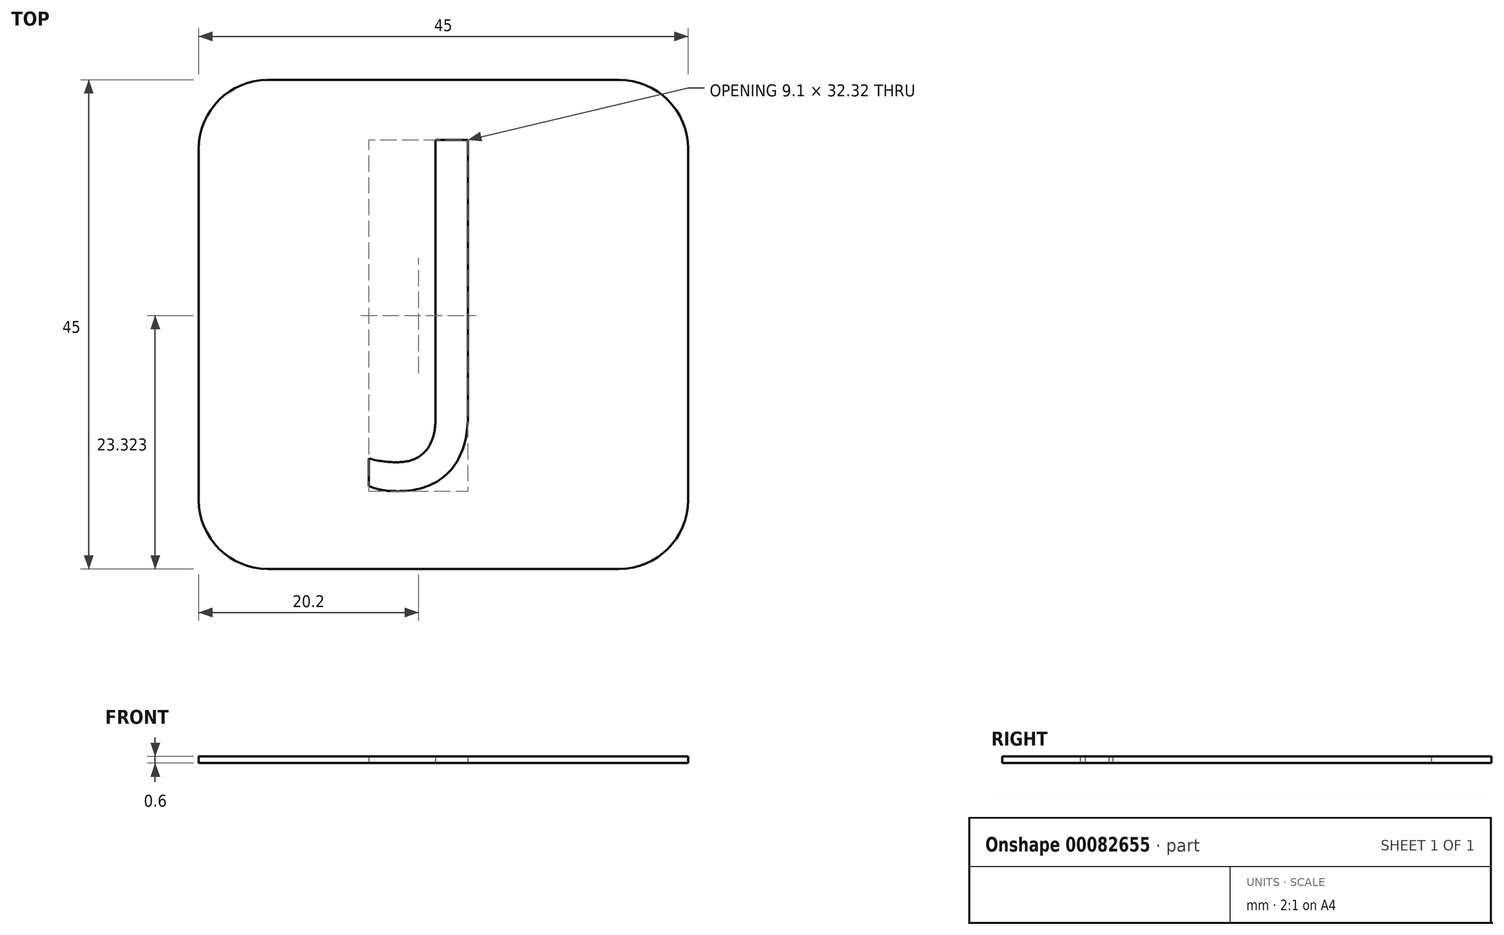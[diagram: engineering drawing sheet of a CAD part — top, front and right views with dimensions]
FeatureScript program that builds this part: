
annotation { "Feature Type Name" : "Feature", "Feature Type Description" : "" }
export const myFeature = defineFeature(function(context is Context, id is Id, definition is map)
    precondition{}
    {
        {
            var Q0;
            Q0=qCreatedBy(makeId("Top.planeOp"),FACE);
            var sketch = newSketch(context, id + "F0", { "sketchPlane" : qUnion([Q0])});
            skLineSegment(sketch, "E0.bottom", {"start": v(0, 0) * mm, "end": v(0, 0) * mm});
            skLineSegment(sketch, "E0.top", {"start": v(0, 0) * mm, "end": v(0, 0) * mm});
            skLineSegment(sketch, "E0.left", {"start": v(0, 0) * mm, "end": v(0, 0) * mm});
            skLineSegment(sketch, "E0.right", {"start": v(0, 0) * mm, "end": v(0, 0) * mm});
            skLineSegment(sketch, "E1.bottom", {"start": v(16.15, 22.5) * mm, "end": v(-16.15, 22.5) * mm});
            skLineSegment(sketch, "E1.top", {"start": v(16.15, -22.5) * mm, "end": v(-16.15, -22.5) * mm});
            skLineSegment(sketch, "E1.left", {"start": v(22.5, 16.15) * mm, "end": v(22.5, -16.15) * mm});
            skLineSegment(sketch, "E1.right", {"start": v(-22.5, 16.15) * mm, "end": v(-22.5, -16.15) * mm});
            skPoint(sketch, "E1.middle", {"position": v(0, 0) * mm});
            skPoint(sketch, "E2.visualSharp", {"position": v(-22.5, 22.5) * mm});
            skArc(sketch, "E2.filletArc", {"start": v(-16.15, 22.5) * mm, "mid": v(-20.64, 20.64) * mm, "end": v(-22.5, 16.15) * mm});
            skPoint(sketch, "E3.visualSharp", {"position": v(22.5, 22.5) * mm});
            skArc(sketch, "E3.filletArc", {"start": v(22.5, 16.15) * mm, "mid": v(20.64, 20.64) * mm, "end": v(16.15, 22.5) * mm});
            skPoint(sketch, "E4.visualSharp", {"position": v(22.5, -22.5) * mm});
            skArc(sketch, "E4.filletArc", {"start": v(16.15, -22.5) * mm, "mid": v(20.64, -20.64) * mm, "end": v(22.5, -16.15) * mm});
            skPoint(sketch, "E5.visualSharp", {"position": v(-22.5, -22.5) * mm});
            skArc(sketch, "E5.filletArc", {"start": v(-22.5, -16.15) * mm, "mid": v(-20.64, -20.64) * mm, "end": v(-16.15, -22.5) * mm});
            skText(sketch, "E6", { "text": "J", "fontName": "OpenSans-Regular.ttf"});
            const initialGuessF0  = {"E6": [-0.00405, -0.0086, 1, 0, 0.0258]};
            skSetInitialGuess(sketch, initialGuessF0);
            skSolve(sketch);
        }
        {
            var Q0;
            Q0 = qSketchRegion(id + "F0", true);
            extrude(context, id + "F2", {"entities" : qUnion([Q0]), "depth" : 0.6 * mm});
        }
    });
